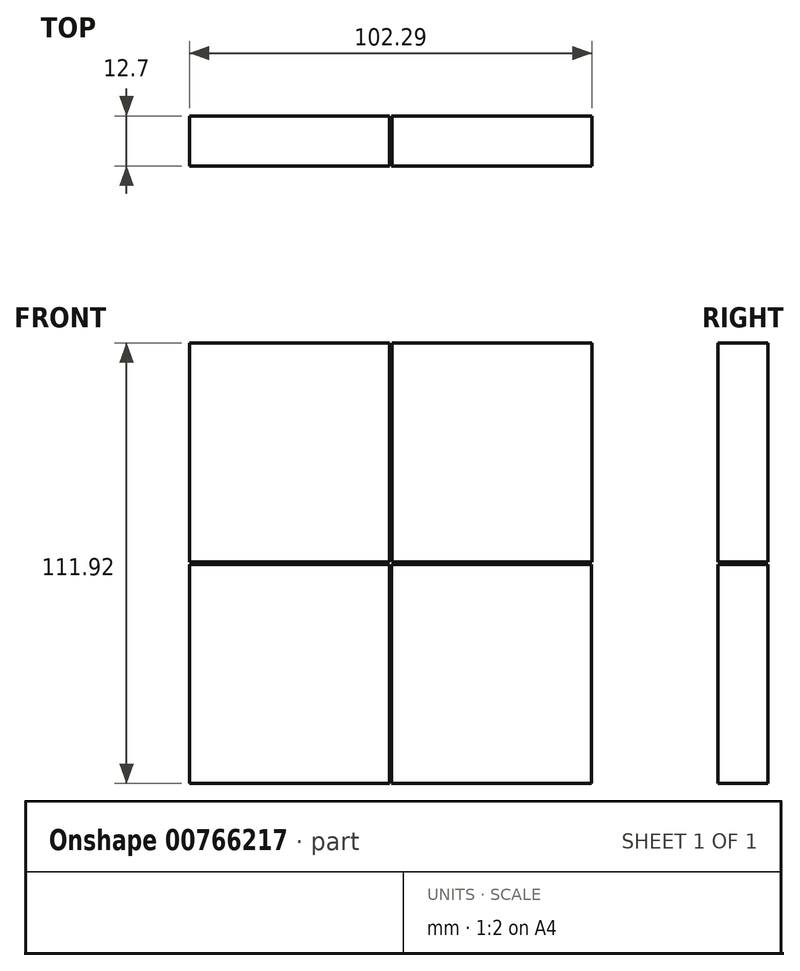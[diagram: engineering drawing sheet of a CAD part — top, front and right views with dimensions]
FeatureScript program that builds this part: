
annotation { "Feature Type Name" : "Feature", "Feature Type Description" : "" }
export const myFeature = defineFeature(function(context is Context, id is Id, definition is map)
    precondition{}
    {
        {
            var Q0;
            Q0=qCreatedBy(makeId("Front.planeOp"),FACE);
            var sketch = newSketch(context, id + "F0", { "sketchPlane" : qUnion([Q0])});
            skLineSegment(sketch, "E0.bottom", {"start": v(-42.35, -20.7) * mm, "end": v(8.43, -20.7) * mm});
            skLineSegment(sketch, "E0.top", {"start": v(-42.35, 34.93) * mm, "end": v(8.43, 34.93) * mm});
            skLineSegment(sketch, "E0.left", {"start": v(-42.35, -20.7) * mm, "end": v(-42.35, 34.93) * mm});
            skLineSegment(sketch, "E0.right", {"start": v(8.43, -20.7) * mm, "end": v(8.43, 34.93) * mm});
            skLineSegment(sketch, "E1.bottom", {"start": v(-93.86, -20.7) * mm, "end": v(-43.06, -20.7) * mm});
            skLineSegment(sketch, "E1.top", {"start": v(-93.86, 34.92) * mm, "end": v(-43.06, 34.92) * mm});
            skLineSegment(sketch, "E1.left", {"start": v(-93.86, -20.7) * mm, "end": v(-93.86, 34.92) * mm});
            skLineSegment(sketch, "E1.right", {"start": v(-43.06, -20.7) * mm, "end": v(-43.06, 34.92) * mm});
            skLineSegment(sketch, "E2.bottom", {"start": v(-42.47, -76.99) * mm, "end": v(8.31, -76.99) * mm});
            skLineSegment(sketch, "E2.top", {"start": v(-42.47, -21.36) * mm, "end": v(8.31, -21.36) * mm});
            skLineSegment(sketch, "E2.left", {"start": v(-42.47, -76.99) * mm, "end": v(-42.47, -21.36) * mm});
            skLineSegment(sketch, "E2.right", {"start": v(8.31, -76.99) * mm, "end": v(8.31, -21.36) * mm});
            skPoint(sketch, "E2.middle", {"position": v(-17.08, -49.17) * mm});
            skLineSegment(sketch, "E3.bottom", {"start": v(-93.82, -76.99) * mm, "end": v(-43.02, -76.99) * mm});
            skLineSegment(sketch, "E3.top", {"start": v(-93.82, -21.37) * mm, "end": v(-43.02, -21.37) * mm});
            skLineSegment(sketch, "E3.left", {"start": v(-93.82, -76.99) * mm, "end": v(-93.82, -21.37) * mm});
            skPoint(sketch, "E3.middle", {"position": v(-68.42, -49.18) * mm});
            skLineSegment(sketch, "E4", {"start": v(-43.02, -21.37) * mm, "end": v(-43.02, -76.99) * mm});
            skSolve(sketch);
        }
        {
            var Q0;
            Q0=qSketchRegion(id+"F0",true);
            extrude(context, id + "F1", {"entities" : qUnion([Q0]), "depth" : 12.7 * mm, "offsetDistance" : 25.4 * mm});
        }
    });
